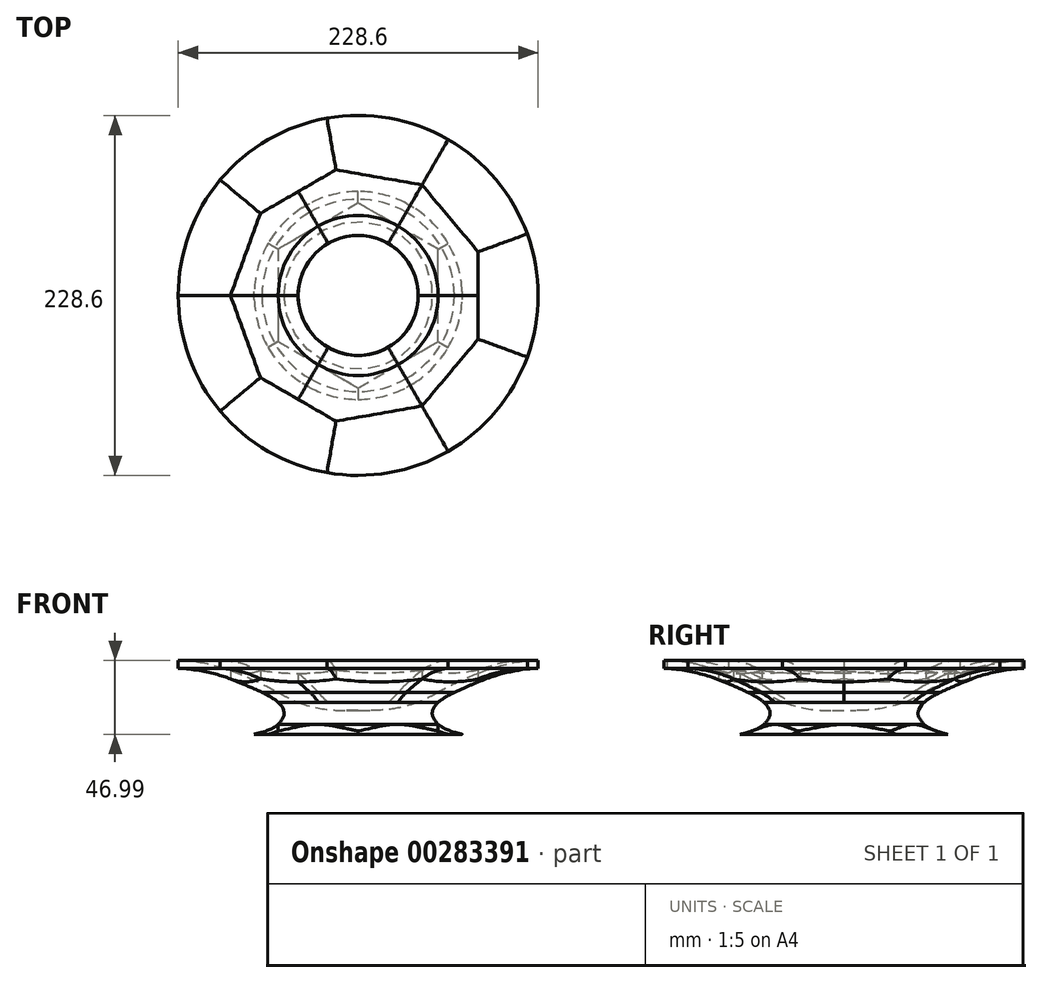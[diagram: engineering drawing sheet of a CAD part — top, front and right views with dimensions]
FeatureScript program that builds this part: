
annotation { "Feature Type Name" : "Feature", "Feature Type Description" : "" }
export const myFeature = defineFeature(function(context is Context, id is Id, definition is map)
    precondition{}
    {
        {
            var Q0;
            Q0=qCreatedBy(makeId("Top.planeOp"),FACE);
            var sketch = newSketch(context, id + "F0", { "sketchPlane" : qUnion([Q0])});
            skLineSegment(sketch, "E0", {"start": v(0, 0) * mm, "end": v(114.3, 0) * mm, "construction": true});
            skCircle(sketch, "E1.cCircle", {"center": v(0, 0) * mm, "radius": 114.3 * mm, "construction": true});
            skLineSegment(sketch, "E1.0", {"start": v(114.3, 41.6) * mm, "end": v(114.3, -41.6) * mm});
            skLineSegment(sketch, "E1.1", {"start": v(114.3, -41.6) * mm, "end": v(60.82, -105.34) * mm});
            skLineSegment(sketch, "E1.2", {"start": v(60.82, -105.34) * mm, "end": v(-21.12, -119.79) * mm});
            skLineSegment(sketch, "E1.3", {"start": v(-21.12, -119.79) * mm, "end": v(-93.18, -78.19) * mm});
            skLineSegment(sketch, "E1.4", {"start": v(-93.18, -78.19) * mm, "end": v(-121.64, 0) * mm});
            skLineSegment(sketch, "E1.5", {"start": v(-121.64, 0) * mm, "end": v(-93.18, 78.19) * mm});
            skLineSegment(sketch, "E1.6", {"start": v(-93.18, 78.19) * mm, "end": v(-21.12, 119.79) * mm});
            skLineSegment(sketch, "E1.7", {"start": v(-21.12, 119.79) * mm, "end": v(60.82, 105.34) * mm});
            skLineSegment(sketch, "E1.8", {"start": v(60.82, 105.34) * mm, "end": v(114.3, 41.6) * mm});
            skPoint(sketch, "E1.0.midPoint", {"position": v(114.3, 0) * mm});
            skLineSegment(sketch, "E2", {"start": v(114.3, 0) * mm, "end": v(76.2, 0) * mm, "construction": true});
            skCircle(sketch, "E3.cCircle", {"center": v(0, 0) * mm, "radius": 76.2 * mm, "construction": true});
            skLineSegment(sketch, "E3.0", {"start": v(76.2, 27.73) * mm, "end": v(76.2, -27.73) * mm});
            skLineSegment(sketch, "E3.1", {"start": v(76.2, -27.73) * mm, "end": v(40.55, -70.23) * mm});
            skLineSegment(sketch, "E3.2", {"start": v(40.55, -70.23) * mm, "end": v(-14.08, -79.86) * mm});
            skLineSegment(sketch, "E3.3", {"start": v(-14.08, -79.86) * mm, "end": v(-62.12, -52.12) * mm});
            skLineSegment(sketch, "E3.4", {"start": v(-62.12, -52.12) * mm, "end": v(-81.1, 0) * mm});
            skLineSegment(sketch, "E3.5", {"start": v(-81.1, 0) * mm, "end": v(-62.12, 52.12) * mm});
            skLineSegment(sketch, "E3.6", {"start": v(-62.12, 52.12) * mm, "end": v(-14.08, 79.86) * mm});
            skLineSegment(sketch, "E3.7", {"start": v(-14.08, 79.86) * mm, "end": v(40.55, 70.23) * mm});
            skLineSegment(sketch, "E3.8", {"start": v(40.55, 70.23) * mm, "end": v(76.2, 27.73) * mm});
            skPoint(sketch, "E3.0.midPoint", {"position": v(76.2, 0) * mm});
            skLineSegment(sketch, "E4", {"start": v(-21.12, 119.79) * mm, "end": v(-14.08, 79.86) * mm});
            skLineSegment(sketch, "E5", {"start": v(-93.18, 78.19) * mm, "end": v(-62.12, 52.12) * mm});
            skLineSegment(sketch, "E6", {"start": v(40.55, 70.23) * mm, "end": v(60.82, 105.34) * mm});
            skLineSegment(sketch, "E7", {"start": v(76.2, 27.73) * mm, "end": v(114.3, 41.6) * mm});
            skLineSegment(sketch, "E8", {"start": v(76.2, 0) * mm, "end": v(57.15, 0) * mm, "construction": true});
            skLineSegment(sketch, "E9", {"start": v(-62.12, 52.12) * mm, "end": v(-29.12, 33.07) * mm, "construction": true});
            skCircle(sketch, "E10.cCircle", {"center": v(0, 0) * mm, "radius": 48.23 * mm, "construction": true});
            skLineSegment(sketch, "E10.0", {"start": v(-48.23, 0) * mm, "end": v(-24.12, 41.77) * mm});
            skLineSegment(sketch, "E10.1", {"start": v(-24.12, 41.77) * mm, "end": v(24.12, 41.77) * mm});
            skLineSegment(sketch, "E10.2", {"start": v(24.12, 41.77) * mm, "end": v(48.23, 0) * mm});
            skLineSegment(sketch, "E10.3", {"start": v(48.23, 0) * mm, "end": v(24.12, -41.77) * mm});
            skLineSegment(sketch, "E10.4", {"start": v(24.12, -41.77) * mm, "end": v(-24.12, -41.77) * mm});
            skLineSegment(sketch, "E10.5", {"start": v(-24.12, -41.77) * mm, "end": v(-48.23, 0) * mm});
            skLineSegment(sketch, "E11", {"start": v(-81.1, 0) * mm, "end": v(-48.23, 0) * mm});
            skLineSegment(sketch, "E12", {"start": v(-24.12, 41.77) * mm, "end": v(-38.1, 66) * mm});
            skLineSegment(sketch, "E13", {"start": v(24.12, 41.77) * mm, "end": v(40.55, 70.23) * mm});
            skSolve(sketch);
        }
        {
            var Q0;
            Q0=makeQuery(id+"F0.imprint","IMPRINT",FACE,{"disambiguationData":[TD([[makeQuery(id+"F0.imprint","IMPRINT",EDGE,{"derivedFrom":sQuery(id+"F0.wireOp",EDGE,"E1.6")}),-1.0]])]});
            var Q1;
            Q1=makeQuery(id+"F0.imprint","IMPRINT",FACE,{"disambiguationData":[TD([[makeQuery(id+"F0.imprint","IMPRINT",EDGE,{"derivedFrom":sQuery(id+"F0.wireOp",EDGE,"E1.8")}),-1.0]])]});
            extrude(context, id + "F1", {"entities" : qUnion([Q0, Q1]), "depth" : 20.32 * mm, "offsetDistance" : 25.4 * mm});
        }
        {
            var Q0;
            {var subQ1=sQuery(id+"F0.wireOp",EDGE,"E3.5");Q0=makeQuery(id+"F0.imprint","IMPRINT",FACE,{"disambiguationData":[TD([[makeQuery(id+"F0.imprint","IMPRINT",EDGE,{"derivedFrom":subQ1}),-1.0]])]});}
            var Q1;
            Q1=makeQuery(id+"F0.imprint","IMPRINT",FACE,{"disambiguationData":[TD([[makeQuery(id+"F0.imprint","IMPRINT",EDGE,{"derivedFrom":sQuery(id+"F0.wireOp",EDGE,"E1.7")}),-1.0]])]});
            extrude(context, id + "F2", {"entities" : qUnion([Q0, Q1]), "depth" : 20.32 * mm});
        }
        {
            var Q0;
            {var subQ0=sQuery(id+"F0.wireOp",EDGE,"E3.7");Q0=makeQuery(id+"F0.imprint","IMPRINT",FACE,{"disambiguationData":[TD([[makeQuery(id+"F0.imprint","IMPRINT",EDGE,{"derivedFrom":subQ0}),-1.0]])]});}
            extrude(context, id + "F3", {"entities" : qUnion([Q0]), "depth" : 20.32 * mm});
        }
        {
            var Q0;
            Q0=qCreatedBy(makeId("Front.planeOp"),FACE);
            var sketch = newSketch(context, id + "F4", { "sketchPlane" : qUnion([Q0])});
            skLineSegment(sketch, "E14", {"start": v(0, 0) * mm, "end": v(0, 114.3) * mm, "construction": true});
            skSolve(sketch);
        }
        {
            var Q0;
            Q0=qCreatedBy(makeId("Top.planeOp"),FACE);
            var sketch = newSketch(context, id + "F5", { "sketchPlane" : qUnion([Q0])});
            skLineSegment(sketch, "E15", {"start": v(0, 0) * mm, "end": v(76.2, 0) * mm, "construction": true});
            skCircle(sketch, "E16.cCircle", {"center": v(0, 0) * mm, "radius": 76.2 * mm, "construction": true});
            skLineSegment(sketch, "E16.0", {"start": v(76.2, 0) * mm, "end": v(38.1, -66) * mm});
            skLineSegment(sketch, "E16.1", {"start": v(38.1, -66) * mm, "end": v(-38.1, -66) * mm});
            skLineSegment(sketch, "E16.2", {"start": v(-38.1, -66) * mm, "end": v(-76.2, 0) * mm});
            skLineSegment(sketch, "E16.3", {"start": v(-76.2, 0) * mm, "end": v(-38.1, 66) * mm});
            skLineSegment(sketch, "E16.4", {"start": v(-38.1, 66) * mm, "end": v(38.1, 66) * mm});
            skLineSegment(sketch, "E16.5", {"start": v(38.1, 66) * mm, "end": v(76.2, 0) * mm});
            skLineSegment(sketch, "E17", {"start": v(0, 0) * mm, "end": v(38.1, 0) * mm, "construction": true});
            skCircle(sketch, "E18.cCircle", {"center": v(0, 0) * mm, "radius": 38.1 * mm, "construction": true});
            skLineSegment(sketch, "E18.0", {"start": v(38.1, 0) * mm, "end": v(19.05, -33) * mm});
            skLineSegment(sketch, "E18.1", {"start": v(19.05, -33) * mm, "end": v(-19.05, -33) * mm});
            skLineSegment(sketch, "E18.2", {"start": v(-19.05, -33) * mm, "end": v(-38.1, 0) * mm});
            skLineSegment(sketch, "E18.3", {"start": v(-38.1, 0) * mm, "end": v(-19.05, 33) * mm});
            skLineSegment(sketch, "E18.4", {"start": v(-19.05, 33) * mm, "end": v(19.05, 33) * mm});
            skLineSegment(sketch, "E18.5", {"start": v(19.05, 33) * mm, "end": v(38.1, 0) * mm});
            skLineSegment(sketch, "E19", {"start": v(19.05, -33) * mm, "end": v(38.1, -66) * mm});
            skLineSegment(sketch, "E20", {"start": v(38.1, 0) * mm, "end": v(76.2, 0) * mm});
            skLineSegment(sketch, "E21", {"start": v(19.05, 33) * mm, "end": v(38.1, 66) * mm});
            skSolve(sketch);
        }
        {
            var Q0;
            Q0=makeQuery(id+"F5.imprint","IMPRINT",FACE,{"disambiguationData":[TD([[makeQuery(id+"F5.imprint","IMPRINT",EDGE,{"derivedFrom":sQuery(id+"F5.wireOp",EDGE,"E16.0")}),-1.0]])]});
            extrude(context, id + "F6", {"entities" : qUnion([Q0]), "oppositeDirection" : true, "depth" : 6.35 * mm});
        }
        {
            var Q0;
            Q0=makeQuery(id+"F5.imprint","IMPRINT",FACE,{"disambiguationData":[TD([[makeQuery(id+"F5.imprint","IMPRINT",EDGE,{"derivedFrom":sQuery(id+"F5.wireOp",EDGE,"E16.5")}),-1.0]])]});
            extrude(context, id + "F7", {"entities" : qUnion([Q0]), "oppositeDirection" : true, "depth" : 6.35 * mm});
        }
        {
            var Q0;
            Q0=makeQuery(id+"F6.opExtrude","SWEPT_BODY",BODY,{"disambiguationData":[OSD([sQuery(id+"F5.wireOp",EDGE,"E16.0"),sQuery(id+"F5.wireOp",EDGE,"E18.0"),sQuery(id+"F5.wireOp",EDGE,"E19"),sQuery(id+"F5.wireOp",EDGE,"E20")])]});
            var Q1;
            Q1=makeQuery(id+"F7.opExtrude","SWEPT_BODY",BODY,{"disambiguationData":[OSD([sQuery(id+"F5.wireOp",EDGE,"E16.5"),sQuery(id+"F5.wireOp",EDGE,"E18.5"),sQuery(id+"F5.wireOp",EDGE,"E20"),sQuery(id+"F5.wireOp",EDGE,"E21")])]});
            var Q2;
            Q2=sQuery(id+"F4.wireOp",EDGE,"E14");
            transform(context, id + "F8", {"entities" : qUnion([Q0, Q1]), "transformType" : TransformType.ROTATION, "transformAxis" : qUnion([Q2]), "angle" : 60 * degree, "makeCopy" : false});
        }
        {
            var Q0;
            Q0=makeQuery(id+"F2.opExtrude","SWEPT_BODY",BODY,{"disambiguationData":[OSD([sQuery(id+"F0.wireOp",EDGE,"E3.5"),sQuery(id+"F0.wireOp",EDGE,"E3.6"),sQuery(id+"F0.wireOp",EDGE,"201d4f59-2997-49bd-9f8f-c68fa2623fab.3"),sQuery(id+"F0.wireOp",EDGE,"vol62nw5-0ljN-dSfL-tH07-V83CAlSku6MR"),sQuery(id+"F0.wireOp",EDGE,"AOmgBGB9-Bh4F-KEFf-iWFI-fRoqLKZDZUkD")])]});
            var Q1;
            Q1=makeQuery(id+"F1.opExtrude","SWEPT_BODY",BODY,{"disambiguationData":[OSD([sQuery(id+"F0.wireOp",EDGE,"E1.8"),sQuery(id+"F0.wireOp",EDGE,"E3.8"),sQuery(id+"F0.wireOp",EDGE,"E6"),sQuery(id+"F0.wireOp",EDGE,"E7")])]});
            var Q2;
            Q2=makeQuery(id+"F3.opExtrude","SWEPT_BODY",BODY,{"disambiguationData":[OSD([sQuery(id+"F0.wireOp",EDGE,"E3.6"),sQuery(id+"F0.wireOp",EDGE,"E3.7"),sQuery(id+"F0.wireOp",EDGE,"201d4f59-2997-49bd-9f8f-c68fa2623fab.4"),sQuery(id+"F0.wireOp",EDGE,"h17IytfR-Qpnw-Sum6-dVJG-BEsi5LHsENnV"),sQuery(id+"F0.wireOp",EDGE,"vol62nw5-0ljN-dSfL-tH07-V83CAlSku6MR")])]});
            var Q3;
            Q3=makeQuery(id+"F2.opExtrude","SWEPT_BODY",BODY,{"disambiguationData":[OSD([sQuery(id+"F0.wireOp",EDGE,"E1.7"),sQuery(id+"F0.wireOp",EDGE,"E3.7"),sQuery(id+"F0.wireOp",EDGE,"E4"),sQuery(id+"F0.wireOp",EDGE,"E6")])]});
            var Q4;
            Q4=makeQuery(id+"F1.opExtrude","SWEPT_BODY",BODY,{"disambiguationData":[OSD([sQuery(id+"F0.wireOp",EDGE,"E1.6"),sQuery(id+"F0.wireOp",EDGE,"E3.6"),sQuery(id+"F0.wireOp",EDGE,"E4"),sQuery(id+"F0.wireOp",EDGE,"E5")])]});
            var Q5;
            Q5=makeQuery(id+"F6.opExtrude","SWEPT_BODY",BODY,{"disambiguationData":[OSD([sQuery(id+"F5.wireOp",EDGE,"E16.0"),sQuery(id+"F5.wireOp",EDGE,"E18.0"),sQuery(id+"F5.wireOp",EDGE,"E19"),sQuery(id+"F5.wireOp",EDGE,"E20")])]});
            var Q6;
            Q6=makeQuery(id+"F7.opExtrude","SWEPT_BODY",BODY,{"disambiguationData":[OSD([sQuery(id+"F5.wireOp",EDGE,"E16.5"),sQuery(id+"F5.wireOp",EDGE,"E18.5"),sQuery(id+"F5.wireOp",EDGE,"E20"),sQuery(id+"F5.wireOp",EDGE,"E21")])]});
            var Q7;
            Q7=sQuery(id+"F4.wireOp",EDGE,"E14");
            transform(context, id + "F9", {"entities" : qUnion([Q0, Q1, Q2, Q3, Q4, Q5, Q6]), "transformType" : TransformType.ROTATION, "transformAxis" : qUnion([Q7]), "angle" : 120 * degree, "makeCopy" : true});
        }
        {
            var Q0;
            Q0=makeQuery(id+"F2.opExtrude","SWEPT_BODY",BODY,{"disambiguationData":[OSD([sQuery(id+"F0.wireOp",EDGE,"E1.7"),sQuery(id+"F0.wireOp",EDGE,"E3.7"),sQuery(id+"F0.wireOp",EDGE,"E4"),sQuery(id+"F0.wireOp",EDGE,"E6")])]});
            var Q1;
            Q1=makeQuery(id+"F3.opExtrude","SWEPT_BODY",BODY,{"disambiguationData":[OSD([sQuery(id+"F0.wireOp",EDGE,"E3.6"),sQuery(id+"F0.wireOp",EDGE,"E3.7"),sQuery(id+"F0.wireOp",EDGE,"201d4f59-2997-49bd-9f8f-c68fa2623fab.4"),sQuery(id+"F0.wireOp",EDGE,"h17IytfR-Qpnw-Sum6-dVJG-BEsi5LHsENnV"),sQuery(id+"F0.wireOp",EDGE,"vol62nw5-0ljN-dSfL-tH07-V83CAlSku6MR")])]});
            var Q2;
            Q2=makeQuery(id+"F1.opExtrude","SWEPT_BODY",BODY,{"disambiguationData":[OSD([sQuery(id+"F0.wireOp",EDGE,"E1.6"),sQuery(id+"F0.wireOp",EDGE,"E3.6"),sQuery(id+"F0.wireOp",EDGE,"E4"),sQuery(id+"F0.wireOp",EDGE,"E5")])]});
            var Q3;
            Q3=makeQuery(id+"F2.opExtrude","SWEPT_BODY",BODY,{"disambiguationData":[OSD([sQuery(id+"F0.wireOp",EDGE,"E3.5"),sQuery(id+"F0.wireOp",EDGE,"E3.6"),sQuery(id+"F0.wireOp",EDGE,"201d4f59-2997-49bd-9f8f-c68fa2623fab.3"),sQuery(id+"F0.wireOp",EDGE,"vol62nw5-0ljN-dSfL-tH07-V83CAlSku6MR"),sQuery(id+"F0.wireOp",EDGE,"AOmgBGB9-Bh4F-KEFf-iWFI-fRoqLKZDZUkD")])]});
            var Q4;
            Q4=makeQuery(id+"F1.opExtrude","SWEPT_BODY",BODY,{"disambiguationData":[OSD([sQuery(id+"F0.wireOp",EDGE,"E1.8"),sQuery(id+"F0.wireOp",EDGE,"E3.8"),sQuery(id+"F0.wireOp",EDGE,"E6"),sQuery(id+"F0.wireOp",EDGE,"E7")])]});
            var Q5;
            Q5=makeQuery(id+"F6.opExtrude","SWEPT_BODY",BODY,{"disambiguationData":[OSD([sQuery(id+"F5.wireOp",EDGE,"E16.0"),sQuery(id+"F5.wireOp",EDGE,"E18.0"),sQuery(id+"F5.wireOp",EDGE,"E19"),sQuery(id+"F5.wireOp",EDGE,"E20")])]});
            var Q6;
            Q6=makeQuery(id+"F7.opExtrude","SWEPT_BODY",BODY,{"disambiguationData":[OSD([sQuery(id+"F5.wireOp",EDGE,"E16.5"),sQuery(id+"F5.wireOp",EDGE,"E18.5"),sQuery(id+"F5.wireOp",EDGE,"E20"),sQuery(id+"F5.wireOp",EDGE,"E21")])]});
            var Q7;
            Q7=sQuery(id+"F4.wireOp",EDGE,"E14");
            transform(context, id + "F10", {"entities" : qUnion([Q0, Q1, Q2, Q3, Q4, Q5, Q6]), "transformType" : TransformType.ROTATION, "transformAxis" : qUnion([Q7]), "angle" : 120 * degree, "oppositeDirection" : true, "makeCopy" : true});
        }
        {
            var Q0;
            Q0=makeQuery(id+"F9.opPattern","COPY",FACE,{"derivedFrom":makeQuery(id+"F7.opExtrude","CAP_FACE",FACE,{"disambiguationData":[OSD([sQuery(id+"F5.wireOp",EDGE,"E16.5"),sQuery(id+"F5.wireOp",EDGE,"E18.5"),sQuery(id+"F5.wireOp",EDGE,"E20"),sQuery(id+"F5.wireOp",EDGE,"E21")])],"isStart":false}),"instanceName":"1"});
            var sketch = newSketch(context, id + "F11", { "sketchPlane" : qUnion([Q0])});
            skLineSegment(sketch, "E22", {"start": v(-38.1, 66) * mm, "end": v(0, 0) * mm, "construction": true});
            skLineSegment(sketch, "E23", {"start": v(0, 0) * mm, "end": v(50.8, 0) * mm, "construction": true});
            skCircle(sketch, "E24.cCircle", {"center": v(0, 0) * mm, "radius": 50.8 * mm, "construction": true});
            skLineSegment(sketch, "E24.0", {"start": v(50.8, 29.33) * mm, "end": v(50.8, -29.33) * mm});
            skLineSegment(sketch, "E24.1", {"start": v(50.8, -29.33) * mm, "end": v(0, -58.66) * mm});
            skLineSegment(sketch, "E24.2", {"start": v(0, -58.66) * mm, "end": v(-50.8, -29.33) * mm});
            skLineSegment(sketch, "E24.3", {"start": v(-50.8, -29.33) * mm, "end": v(-50.8, 29.33) * mm});
            skLineSegment(sketch, "E24.4", {"start": v(-50.8, 29.33) * mm, "end": v(0, 58.66) * mm});
            skLineSegment(sketch, "E24.5", {"start": v(0, 58.66) * mm, "end": v(50.8, 29.33) * mm});
            skPoint(sketch, "E24.0.midPoint", {"position": v(50.8, 0) * mm});
            skSolve(sketch);
        }
        {
            var Q0;
            Q0 = qSketchRegion(id + "F11", true);
            extrude(context, id + "F12", {"entities" : qUnion([Q0]), "depth" : 20.32 * mm});
        }
        {
            var Q0;
            Q0=makeQuery(id+"F9.opPattern","COPY",BODY,{"derivedFrom":makeQuery(id+"F7.opExtrude","SWEPT_BODY",BODY,{"disambiguationData":[OSD([sQuery(id+"F5.wireOp",EDGE,"E16.5"),sQuery(id+"F5.wireOp",EDGE,"E18.5"),sQuery(id+"F5.wireOp",EDGE,"E20"),sQuery(id+"F5.wireOp",EDGE,"E21")])]}),"instanceName":"1"});
            var Q1;
            Q1=makeQuery(id+"F9.opPattern","COPY",BODY,{"derivedFrom":makeQuery(id+"F6.opExtrude","SWEPT_BODY",BODY,{"disambiguationData":[OSD([sQuery(id+"F5.wireOp",EDGE,"E16.0"),sQuery(id+"F5.wireOp",EDGE,"E18.0"),sQuery(id+"F5.wireOp",EDGE,"E19"),sQuery(id+"F5.wireOp",EDGE,"E20")])]}),"instanceName":"1"});
            var Q2;
            Q2=makeQuery(id+"F7.opExtrude","SWEPT_BODY",BODY,{"disambiguationData":[OSD([sQuery(id+"F5.wireOp",EDGE,"E16.5"),sQuery(id+"F5.wireOp",EDGE,"E18.5"),sQuery(id+"F5.wireOp",EDGE,"E20"),sQuery(id+"F5.wireOp",EDGE,"E21")])]});
            var Q3;
            Q3=makeQuery(id+"F6.opExtrude","SWEPT_BODY",BODY,{"disambiguationData":[OSD([sQuery(id+"F5.wireOp",EDGE,"E16.0"),sQuery(id+"F5.wireOp",EDGE,"E18.0"),sQuery(id+"F5.wireOp",EDGE,"E19"),sQuery(id+"F5.wireOp",EDGE,"E20")])]});
            var Q4;
            Q4=makeQuery(id+"F10.opPattern","COPY",BODY,{"derivedFrom":makeQuery(id+"F7.opExtrude","SWEPT_BODY",BODY,{"disambiguationData":[OSD([sQuery(id+"F5.wireOp",EDGE,"E16.5"),sQuery(id+"F5.wireOp",EDGE,"E18.5"),sQuery(id+"F5.wireOp",EDGE,"E20"),sQuery(id+"F5.wireOp",EDGE,"E21")])]}),"instanceName":"1"});
            var Q5;
            Q5=makeQuery(id+"F10.opPattern","COPY",BODY,{"derivedFrom":makeQuery(id+"F6.opExtrude","SWEPT_BODY",BODY,{"disambiguationData":[OSD([sQuery(id+"F5.wireOp",EDGE,"E16.0"),sQuery(id+"F5.wireOp",EDGE,"E18.0"),sQuery(id+"F5.wireOp",EDGE,"E19"),sQuery(id+"F5.wireOp",EDGE,"E20")])]}),"instanceName":"1"});
            transform(context, id + "F13", {"entities" : qUnion([Q0, Q1, Q2, Q3, Q4, Q5]), "transformType" : TransformType.TRANSLATION_3D, "dx" : 0 * mm, "dy" : 0 * mm, "dz" : -20.32 * mm, "makeCopy" : true});
        }
        {
            var Q0;
            Q0=makeQuery(id+"F13.opPattern","COPY",BODY,{"derivedFrom":makeQuery(id+"F9.opPattern","COPY",BODY,{"derivedFrom":makeQuery(id+"F6.opExtrude","SWEPT_BODY",BODY,{"disambiguationData":[OSD([sQuery(id+"F5.wireOp",EDGE,"E16.0"),sQuery(id+"F5.wireOp",EDGE,"E18.0"),sQuery(id+"F5.wireOp",EDGE,"E19"),sQuery(id+"F5.wireOp",EDGE,"E20")])]}),"instanceName":"1"}),"instanceName":"1"});
            var Q1;
            Q1=makeQuery(id+"F13.opPattern","COPY",BODY,{"derivedFrom":makeQuery(id+"F9.opPattern","COPY",BODY,{"derivedFrom":makeQuery(id+"F7.opExtrude","SWEPT_BODY",BODY,{"disambiguationData":[OSD([sQuery(id+"F5.wireOp",EDGE,"E16.5"),sQuery(id+"F5.wireOp",EDGE,"E18.5"),sQuery(id+"F5.wireOp",EDGE,"E20"),sQuery(id+"F5.wireOp",EDGE,"E21")])]}),"instanceName":"1"}),"instanceName":"1"});
            var Q2;
            Q2=makeQuery(id+"F13.opPattern","COPY",BODY,{"derivedFrom":makeQuery(id+"F10.opPattern","COPY",BODY,{"derivedFrom":makeQuery(id+"F6.opExtrude","SWEPT_BODY",BODY,{"disambiguationData":[OSD([sQuery(id+"F5.wireOp",EDGE,"E16.0"),sQuery(id+"F5.wireOp",EDGE,"E18.0"),sQuery(id+"F5.wireOp",EDGE,"E19"),sQuery(id+"F5.wireOp",EDGE,"E20")])]}),"instanceName":"1"}),"instanceName":"1"});
            var Q3;
            Q3=makeQuery(id+"F13.opPattern","COPY",BODY,{"derivedFrom":makeQuery(id+"F10.opPattern","COPY",BODY,{"derivedFrom":makeQuery(id+"F7.opExtrude","SWEPT_BODY",BODY,{"disambiguationData":[OSD([sQuery(id+"F5.wireOp",EDGE,"E16.5"),sQuery(id+"F5.wireOp",EDGE,"E18.5"),sQuery(id+"F5.wireOp",EDGE,"E20"),sQuery(id+"F5.wireOp",EDGE,"E21")])]}),"instanceName":"1"}),"instanceName":"1"});
            var Q4;
            Q4=makeQuery(id+"F13.opPattern","COPY",BODY,{"derivedFrom":makeQuery(id+"F6.opExtrude","SWEPT_BODY",BODY,{"disambiguationData":[OSD([sQuery(id+"F5.wireOp",EDGE,"E16.0"),sQuery(id+"F5.wireOp",EDGE,"E18.0"),sQuery(id+"F5.wireOp",EDGE,"E19"),sQuery(id+"F5.wireOp",EDGE,"E20")])]}),"instanceName":"1"});
            var Q5;
            Q5=makeQuery(id+"F13.opPattern","COPY",BODY,{"derivedFrom":makeQuery(id+"F7.opExtrude","SWEPT_BODY",BODY,{"disambiguationData":[OSD([sQuery(id+"F5.wireOp",EDGE,"E16.5"),sQuery(id+"F5.wireOp",EDGE,"E18.5"),sQuery(id+"F5.wireOp",EDGE,"E20"),sQuery(id+"F5.wireOp",EDGE,"E21")])]}),"instanceName":"1"});
            var Q6;
            Q6=sQuery(id+"F4.wireOp",EDGE,"E14");
            transform(context, id + "F14", {"entities" : qUnion([Q0, Q1, Q2, Q3, Q4, Q5]), "transformType" : TransformType.ROTATION, "transformAxis" : qUnion([Q6]), "angle" : 30 * degree, "makeCopy" : false});
        }
        {
            var Q0;
            Q0=makeQuery(id+"F12.opExtrude","SWEPT_BODY",BODY,{"disambiguationData":[OSD([sQuery(id+"F11.wireOp",EDGE,"E24.0"),sQuery(id+"F11.wireOp",EDGE,"E24.1"),sQuery(id+"F11.wireOp",EDGE,"E24.2"),sQuery(id+"F11.wireOp",EDGE,"E24.3"),sQuery(id+"F11.wireOp",EDGE,"E24.4"),sQuery(id+"F11.wireOp",EDGE,"E24.5")])]});
            var Q1;
            Q1=makeQuery(id+"F13.opPattern","COPY",BODY,{"derivedFrom":makeQuery(id+"F9.opPattern","COPY",BODY,{"derivedFrom":makeQuery(id+"F7.opExtrude","SWEPT_BODY",BODY,{"disambiguationData":[OSD([sQuery(id+"F5.wireOp",EDGE,"E16.5"),sQuery(id+"F5.wireOp",EDGE,"E18.5"),sQuery(id+"F5.wireOp",EDGE,"E20"),sQuery(id+"F5.wireOp",EDGE,"E21")])]}),"instanceName":"1"}),"instanceName":"1"});
            var Q2;
            Q2=makeQuery(id+"F13.opPattern","COPY",BODY,{"derivedFrom":makeQuery(id+"F10.opPattern","COPY",BODY,{"derivedFrom":makeQuery(id+"F6.opExtrude","SWEPT_BODY",BODY,{"disambiguationData":[OSD([sQuery(id+"F5.wireOp",EDGE,"E16.0"),sQuery(id+"F5.wireOp",EDGE,"E18.0"),sQuery(id+"F5.wireOp",EDGE,"E19"),sQuery(id+"F5.wireOp",EDGE,"E20")])]}),"instanceName":"1"}),"instanceName":"1"});
            var Q3;
            Q3=makeQuery(id+"F13.opPattern","COPY",BODY,{"derivedFrom":makeQuery(id+"F10.opPattern","COPY",BODY,{"derivedFrom":makeQuery(id+"F7.opExtrude","SWEPT_BODY",BODY,{"disambiguationData":[OSD([sQuery(id+"F5.wireOp",EDGE,"E16.5"),sQuery(id+"F5.wireOp",EDGE,"E18.5"),sQuery(id+"F5.wireOp",EDGE,"E20"),sQuery(id+"F5.wireOp",EDGE,"E21")])]}),"instanceName":"1"}),"instanceName":"1"});
            var Q4;
            Q4=makeQuery(id+"F13.opPattern","COPY",BODY,{"derivedFrom":makeQuery(id+"F6.opExtrude","SWEPT_BODY",BODY,{"disambiguationData":[OSD([sQuery(id+"F5.wireOp",EDGE,"E16.0"),sQuery(id+"F5.wireOp",EDGE,"E18.0"),sQuery(id+"F5.wireOp",EDGE,"E19"),sQuery(id+"F5.wireOp",EDGE,"E20")])]}),"instanceName":"1"});
            var Q5;
            Q5=makeQuery(id+"F13.opPattern","COPY",BODY,{"derivedFrom":makeQuery(id+"F7.opExtrude","SWEPT_BODY",BODY,{"disambiguationData":[OSD([sQuery(id+"F5.wireOp",EDGE,"E16.5"),sQuery(id+"F5.wireOp",EDGE,"E18.5"),sQuery(id+"F5.wireOp",EDGE,"E20"),sQuery(id+"F5.wireOp",EDGE,"E21")])]}),"instanceName":"1"});
            var Q6;
            Q6=makeQuery(id+"F13.opPattern","COPY",BODY,{"derivedFrom":makeQuery(id+"F9.opPattern","COPY",BODY,{"derivedFrom":makeQuery(id+"F6.opExtrude","SWEPT_BODY",BODY,{"disambiguationData":[OSD([sQuery(id+"F5.wireOp",EDGE,"E16.0"),sQuery(id+"F5.wireOp",EDGE,"E18.0"),sQuery(id+"F5.wireOp",EDGE,"E19"),sQuery(id+"F5.wireOp",EDGE,"E20")])]}),"instanceName":"1"}),"instanceName":"1"});
            booleanBodies(context, id + "F15", {"operationType" : BooleanOperationType.SUBTRACTION, "tools" : qUnion([Q0]), "targets" : qUnion([Q1, Q2, Q3, Q4, Q5, Q6]), "keepTools" : true});
        }
        {
            var Q0;
            Q0=qCreatedBy(makeId("Right.planeOp"),FACE);
            var sketch = newSketch(context, id + "F16", { "sketchPlane" : qUnion([Q0])});
            skLineSegment(sketch, "E25", {"start": v(0, 0) * mm, "end": v(-114.3, 0) * mm, "construction": true});
            skLineSegment(sketch, "E26", {"start": v(-114.3, 0) * mm, "end": v(-114.3, 20.32) * mm, "construction": true});
            skLineSegment(sketch, "E27", {"start": v(-114.3, 20.32) * mm, "end": v(-50.8, 20.32) * mm, "construction": true});
            skLineSegment(sketch, "E28", {"start": v(-50.8, 20.32) * mm, "end": v(-50.8, 0) * mm, "construction": true});
            skLineSegment(sketch, "E29", {"start": v(-50.8, 0) * mm, "end": v(-38.1, 0) * mm, "construction": true});
            skLineSegment(sketch, "E30", {"start": v(-38.1, 0) * mm, "end": v(-38.1, -6.35) * mm, "construction": true});
            skLineSegment(sketch, "E31", {"start": v(-38.1, -6.35) * mm, "end": v(-38.1, -26.67) * mm, "construction": true});
            skLineSegment(sketch, "E32", {"start": v(-38.1, -26.67) * mm, "end": v(-63.5, -26.67) * mm, "construction": true});
            skLineSegment(sketch, "E33", {"start": v(-63.5, -26.67) * mm, "end": v(-63.5, -20.32) * mm, "construction": true});
            skLineSegment(sketch, "E34", {"start": v(-63.5, -20.32) * mm, "end": v(-50.8, -20.32) * mm, "construction": true});
            skLineSegment(sketch, "E35", {"start": v(-50.8, -20.32) * mm, "end": v(-50.8, -6.35) * mm, "construction": true});
            skLineSegment(sketch, "E36", {"start": v(-114.3, 20.32) * mm, "end": v(-114.3, 15.24) * mm, "construction": true});
            skFitSpline(sketch, "E37", {"points": [v(-50.8, -20.32) * mm, v(-47.07, -14.19) * mm, v(-50.8, -6.35) * mm, v(-70.87, 4.38) * mm, v(-85.96, 10.28) * mm, v(-114.3, 15.24) * mm], "startDerivative": vector(37.86, 43.28) * mm, "endDerivative": vector(-120.47, 2.36) * mm});
            skLineSegment(sketch, "E38", {"start": v(-38.1, -6.35) * mm, "end": v(0, -6.35) * mm, "construction": true});
            skLineSegment(sketch, "E39", {"start": v(0, -6.35) * mm, "end": v(0, -11.43) * mm, "construction": true});
            skFitSpline(sketch, "E40", {"points": [v(-114.3, 20.32) * mm, v(-71.06, 9.96) * mm, v(-50.8, 0) * mm, v(-38.1, -6.35) * mm, v(-21.02, -10.68) * mm, v(0, -11.43) * mm], "startDerivative": vector(181.54, 0) * mm, "endDerivative": vector(157.86, 2.62) * mm});
            skLineSegment(sketch, "E41", {"start": v(-38.1, -26.67) * mm, "end": v(-66.04, -26.67) * mm, "construction": true});
            skFitSpline(sketch, "E42", {"points": [v(-50.8, -20.32) * mm, v(-66.04, -26.67) * mm], "startDerivative": vector(-11.2, -9.67) * mm, "endDerivative": vector(-18.41, -4.56) * mm});
            skLineSegment(sketch, "E43", {"start": v(-66.04, -26.67) * mm, "end": v(0, -26.67) * mm});
            skLineSegment(sketch, "E44", {"start": v(0, -26.67) * mm, "end": v(0, -11.43) * mm});
            skLineSegment(sketch, "E45", {"start": v(-114.3, 20.32) * mm, "end": v(-114.3, 15.24) * mm});
            skSolve(sketch);
        }
        {
            var Q0;
            Q0 = qSketchRegion(id + "F16", true);
            var Q1;
            Q1=sQuery(id+"F4.wireOp",EDGE,"E14");
            revolve(context, id + "F17", {"entities" : qUnion([Q0]), "axis" : qUnion([Q1]), "revolveType" : RevolveType.FULL});
        }
        {
            var Q0;
            Q0=makeQuery(id+"F17.opRevolve","SWEPT_BODY",BODY,{"disambiguationData":[OSD([sQuery(id+"F16.wireOp",EDGE,"E37"),sQuery(id+"F16.wireOp",EDGE,"E40"),sQuery(id+"F16.wireOp",EDGE,"E42"),sQuery(id+"F16.wireOp",EDGE,"E43"),sQuery(id+"F16.wireOp",EDGE,"E44"),sQuery(id+"F16.wireOp",EDGE,"E45")])]});
            transform(context, id + "F18", {"entities" : qUnion([Q0]), "transformType" : TransformType.TRANSLATION_3D, "dx" : 0 * mm, "dy" : 304.8 * mm, "dz" : 0 * mm, "makeCopy" : false});
        }
        {
            var Q0;
            Q0=makeQuery(id+"F17.opRevolve","SWEPT_FACE",FACE,{"disambiguationData":[OSD([sQuery(id+"F16.wireOp",EDGE,"E43")])]});
            var sketch = newSketch(context, id + "F19", { "sketchPlane" : qUnion([Q0])});
            skLineSegment(sketch, "E46.bottom", {"start": v(-152.4, -155.9) * mm, "end": v(152.4, -155.9) * mm});
            skLineSegment(sketch, "E46.top", {"start": v(-152.4, 148.9) * mm, "end": v(152.4, 148.9) * mm});
            skLineSegment(sketch, "E46.left", {"start": v(-152.4, -155.9) * mm, "end": v(-152.4, 148.9) * mm});
            skLineSegment(sketch, "E46.right", {"start": v(152.4, -155.9) * mm, "end": v(152.4, 148.9) * mm});
            skPoint(sketch, "E46.middle", {"position": v(0, -3.5) * mm});
            skSolve(sketch);
        }
        {
            var Q0;
            Q0=makeQuery(id+"F19.imprint","IMPRINT",FACE,{"disambiguationData":[TD([[makeQuery(id+"F19.imprint","IMPRINT",EDGE,{"derivedFrom":sQuery(id+"F19.wireOp",EDGE,"E46.bottom")}),1.0]])]});
            extrude(context, id + "F20", {"entities" : qUnion([Q0]), "oppositeDirection" : true, "depth" : 47 * mm});
        }
        {
            var Q0;
            Q0=makeQuery(id+"F22.opBoolean","SPLIT",BODY,{"disambiguationData":[OD(0.0)],"derivedFrom":makeQuery(id+"F20.opExtrude","SWEPT_BODY",BODY,{"disambiguationData":[OSD([sQuery(id+"F16.wireOp",EDGE,"E42"),sQuery(id+"F16.wireOp",EDGE,"E43"),sQuery(id+"F19.wireOp",EDGE,"E46.bottom"),sQuery(id+"F19.wireOp",EDGE,"E46.top"),sQuery(id+"F19.wireOp",EDGE,"E46.left"),sQuery(id+"F19.wireOp",EDGE,"E46.right")])]})});
            var Q1;
            Q1=makeQuery(id+"F22.opBoolean","SPLIT",BODY,{"disambiguationData":[OD(1.0)],"derivedFrom":makeQuery(id+"F20.opExtrude","SWEPT_BODY",BODY,{"disambiguationData":[OSD([sQuery(id+"F16.wireOp",EDGE,"E42"),sQuery(id+"F16.wireOp",EDGE,"E43"),sQuery(id+"F19.wireOp",EDGE,"E46.bottom"),sQuery(id+"F19.wireOp",EDGE,"E46.top"),sQuery(id+"F19.wireOp",EDGE,"E46.left"),sQuery(id+"F19.wireOp",EDGE,"E46.right")])]})});
            transform(context, id + "F21", {"entities" : qUnion([Q0, Q1]), "transformType" : TransformType.TRANSLATION_3D, "dx" : 0 * mm, "dy" : 304.8 * mm, "dz" : 0 * mm, "makeCopy" : false});
        }
        {
            var Q0;
            Q0=makeQuery(id+"F17.opRevolve","SWEPT_BODY",BODY,{"disambiguationData":[OSD([sQuery(id+"F16.wireOp",EDGE,"E37"),sQuery(id+"F16.wireOp",EDGE,"E40"),sQuery(id+"F16.wireOp",EDGE,"E42"),sQuery(id+"F16.wireOp",EDGE,"E43"),sQuery(id+"F16.wireOp",EDGE,"E44"),sQuery(id+"F16.wireOp",EDGE,"E45")])]});
            var Q1;
            Q1=makeQuery(id+"F20.opExtrude","SWEPT_BODY",BODY,{"disambiguationData":[OSD([sQuery(id+"F19.wireOp",EDGE,"E46.bottom"),sQuery(id+"F19.wireOp",EDGE,"E46.top"),sQuery(id+"F19.wireOp",EDGE,"E46.left"),sQuery(id+"F19.wireOp",EDGE,"E46.right")])]});
            booleanBodies(context, id + "F22", {"operationType" : BooleanOperationType.SUBTRACTION, "tools" : qUnion([Q0]), "targets" : qUnion([Q1])});
        }
        {
            var Q0;
            Q0=makeQuery(id+"F22.opBoolean","SPLIT",BODY,{"disambiguationData":[OD(1.0)],"derivedFrom":makeQuery(id+"F20.opExtrude","SWEPT_BODY",BODY,{"disambiguationData":[OSD([sQuery(id+"F19.wireOp",EDGE,"E46.bottom"),sQuery(id+"F19.wireOp",EDGE,"E46.top"),sQuery(id+"F19.wireOp",EDGE,"E46.left"),sQuery(id+"F19.wireOp",EDGE,"E46.right")])]})});
            var Q1;
            Q1=makeQuery(id+"F22.opBoolean","SPLIT",BODY,{"disambiguationData":[OD(0.0)],"derivedFrom":makeQuery(id+"F20.opExtrude","SWEPT_BODY",BODY,{"disambiguationData":[OSD([sQuery(id+"F19.wireOp",EDGE,"E46.bottom"),sQuery(id+"F19.wireOp",EDGE,"E46.top"),sQuery(id+"F19.wireOp",EDGE,"E46.left"),sQuery(id+"F19.wireOp",EDGE,"E46.right")])]})});
            transform(context, id + "F23", {"entities" : qUnion([Q0, Q1]), "transformType" : TransformType.TRANSLATION_3D, "dx" : 0 * mm, "dy" : -304.8 * mm, "dz" : 0 * mm, "makeCopy" : false});
        }
        {
            var Q0;
            Q0=makeQuery(id+"F22.opBoolean","SPLIT",BODY,{"disambiguationData":[OD(1.0)],"derivedFrom":makeQuery(id+"F20.opExtrude","SWEPT_BODY",BODY,{"disambiguationData":[OSD([sQuery(id+"F16.wireOp",EDGE,"E42"),sQuery(id+"F16.wireOp",EDGE,"E43"),sQuery(id+"F19.wireOp",EDGE,"E46.bottom"),sQuery(id+"F19.wireOp",EDGE,"E46.top"),sQuery(id+"F19.wireOp",EDGE,"E46.left"),sQuery(id+"F19.wireOp",EDGE,"E46.right")])]})});
            var Q1;
            Q1=makeQuery(id+"F22.opBoolean","SPLIT",BODY,{"disambiguationData":[OD(0.0)],"derivedFrom":makeQuery(id+"F20.opExtrude","SWEPT_BODY",BODY,{"disambiguationData":[OSD([sQuery(id+"F16.wireOp",EDGE,"E42"),sQuery(id+"F16.wireOp",EDGE,"E43"),sQuery(id+"F19.wireOp",EDGE,"E46.bottom"),sQuery(id+"F19.wireOp",EDGE,"E46.top"),sQuery(id+"F19.wireOp",EDGE,"E46.left"),sQuery(id+"F19.wireOp",EDGE,"E46.right")])]})});
            var Q2;
            Q2=makeQuery(id+"F1.opExtrude","SWEPT_BODY",BODY,{"disambiguationData":[OSD([sQuery(id+"F0.wireOp",EDGE,"E1.6"),sQuery(id+"F0.wireOp",EDGE,"E3.6"),sQuery(id+"F0.wireOp",EDGE,"E4"),sQuery(id+"F0.wireOp",EDGE,"E5")])]});
            var Q3;
            Q3=makeQuery(id+"F13.opPattern","COPY",BODY,{"derivedFrom":makeQuery(id+"F10.opPattern","COPY",BODY,{"derivedFrom":makeQuery(id+"F7.opExtrude","SWEPT_BODY",BODY,{"disambiguationData":[OSD([sQuery(id+"F5.wireOp",EDGE,"E16.5"),sQuery(id+"F5.wireOp",EDGE,"E18.5"),sQuery(id+"F5.wireOp",EDGE,"E20"),sQuery(id+"F5.wireOp",EDGE,"E21")])]}),"instanceName":"1"}),"instanceName":"1"});
            var Q4;
            Q4=makeQuery(id+"F13.opPattern","COPY",BODY,{"derivedFrom":makeQuery(id+"F9.opPattern","COPY",BODY,{"derivedFrom":makeQuery(id+"F6.opExtrude","SWEPT_BODY",BODY,{"disambiguationData":[OSD([sQuery(id+"F5.wireOp",EDGE,"E16.0"),sQuery(id+"F5.wireOp",EDGE,"E18.0"),sQuery(id+"F5.wireOp",EDGE,"E19"),sQuery(id+"F5.wireOp",EDGE,"E20")])]}),"instanceName":"1"}),"instanceName":"1"});
            var Q5;
            Q5=makeQuery(id+"F13.opPattern","COPY",BODY,{"derivedFrom":makeQuery(id+"F9.opPattern","COPY",BODY,{"derivedFrom":makeQuery(id+"F7.opExtrude","SWEPT_BODY",BODY,{"disambiguationData":[OSD([sQuery(id+"F5.wireOp",EDGE,"E16.5"),sQuery(id+"F5.wireOp",EDGE,"E18.5"),sQuery(id+"F5.wireOp",EDGE,"E20"),sQuery(id+"F5.wireOp",EDGE,"E21")])]}),"instanceName":"1"}),"instanceName":"1"});
            var Q6;
            Q6=makeQuery(id+"F13.opPattern","COPY",BODY,{"derivedFrom":makeQuery(id+"F10.opPattern","COPY",BODY,{"derivedFrom":makeQuery(id+"F6.opExtrude","SWEPT_BODY",BODY,{"disambiguationData":[OSD([sQuery(id+"F5.wireOp",EDGE,"E16.0"),sQuery(id+"F5.wireOp",EDGE,"E18.0"),sQuery(id+"F5.wireOp",EDGE,"E19"),sQuery(id+"F5.wireOp",EDGE,"E20")])]}),"instanceName":"1"}),"instanceName":"1"});
            var Q7;
            Q7=makeQuery(id+"F13.opPattern","COPY",BODY,{"derivedFrom":makeQuery(id+"F7.opExtrude","SWEPT_BODY",BODY,{"disambiguationData":[OSD([sQuery(id+"F5.wireOp",EDGE,"E16.5"),sQuery(id+"F5.wireOp",EDGE,"E18.5"),sQuery(id+"F5.wireOp",EDGE,"E20"),sQuery(id+"F5.wireOp",EDGE,"E21")])]}),"instanceName":"1"});
            var Q8;
            Q8=makeQuery(id+"F3.opExtrude","SWEPT_BODY",BODY,{"disambiguationData":[OSD([sQuery(id+"F0.wireOp",EDGE,"E3.6"),sQuery(id+"F0.wireOp",EDGE,"E3.7"),sQuery(id+"F0.wireOp",EDGE,"E10.1"),sQuery(id+"F0.wireOp",EDGE,"E12"),sQuery(id+"F0.wireOp",EDGE,"E13")])]});
            var Q9;
            Q9=makeQuery(id+"F6.opExtrude","SWEPT_BODY",BODY,{"disambiguationData":[OSD([sQuery(id+"F5.wireOp",EDGE,"E16.0"),sQuery(id+"F5.wireOp",EDGE,"E18.0"),sQuery(id+"F5.wireOp",EDGE,"E19"),sQuery(id+"F5.wireOp",EDGE,"E20")])]});
            var Q10;
            Q10=makeQuery(id+"F7.opExtrude","SWEPT_BODY",BODY,{"disambiguationData":[OSD([sQuery(id+"F5.wireOp",EDGE,"E16.5"),sQuery(id+"F5.wireOp",EDGE,"E18.5"),sQuery(id+"F5.wireOp",EDGE,"E20"),sQuery(id+"F5.wireOp",EDGE,"E21")])]});
            var Q11;
            Q11=makeQuery(id+"F9.opPattern","COPY",BODY,{"derivedFrom":makeQuery(id+"F1.opExtrude","SWEPT_BODY",BODY,{"disambiguationData":[OSD([sQuery(id+"F0.wireOp",EDGE,"E1.6"),sQuery(id+"F0.wireOp",EDGE,"E3.6"),sQuery(id+"F0.wireOp",EDGE,"E4"),sQuery(id+"F0.wireOp",EDGE,"E5")])]}),"instanceName":"1"});
            var Q12;
            Q12=makeQuery(id+"F9.opPattern","COPY",BODY,{"derivedFrom":makeQuery(id+"F1.opExtrude","SWEPT_BODY",BODY,{"disambiguationData":[OSD([sQuery(id+"F0.wireOp",EDGE,"E1.8"),sQuery(id+"F0.wireOp",EDGE,"E3.8"),sQuery(id+"F0.wireOp",EDGE,"E6"),sQuery(id+"F0.wireOp",EDGE,"E7")])]}),"instanceName":"1"});
            var Q13;
            Q13=makeQuery(id+"F9.opPattern","COPY",BODY,{"derivedFrom":makeQuery(id+"F2.opExtrude","SWEPT_BODY",BODY,{"disambiguationData":[OSD([sQuery(id+"F0.wireOp",EDGE,"E1.7"),sQuery(id+"F0.wireOp",EDGE,"E3.7"),sQuery(id+"F0.wireOp",EDGE,"E4"),sQuery(id+"F0.wireOp",EDGE,"E6")])]}),"instanceName":"1"});
            var Q14;
            Q14=makeQuery(id+"F9.opPattern","COPY",BODY,{"derivedFrom":makeQuery(id+"F2.opExtrude","SWEPT_BODY",BODY,{"disambiguationData":[OSD([sQuery(id+"F0.wireOp",EDGE,"E3.5"),sQuery(id+"F0.wireOp",EDGE,"E3.6"),sQuery(id+"F0.wireOp",EDGE,"E10.0"),sQuery(id+"F0.wireOp",EDGE,"E11"),sQuery(id+"F0.wireOp",EDGE,"E12")])]}),"instanceName":"1"});
            var Q15;
            Q15=makeQuery(id+"F9.opPattern","COPY",BODY,{"derivedFrom":makeQuery(id+"F3.opExtrude","SWEPT_BODY",BODY,{"disambiguationData":[OSD([sQuery(id+"F0.wireOp",EDGE,"E3.6"),sQuery(id+"F0.wireOp",EDGE,"E3.7"),sQuery(id+"F0.wireOp",EDGE,"E10.1"),sQuery(id+"F0.wireOp",EDGE,"E12"),sQuery(id+"F0.wireOp",EDGE,"E13")])]}),"instanceName":"1"});
            var Q16;
            Q16=makeQuery(id+"F9.opPattern","COPY",BODY,{"derivedFrom":makeQuery(id+"F6.opExtrude","SWEPT_BODY",BODY,{"disambiguationData":[OSD([sQuery(id+"F5.wireOp",EDGE,"E16.0"),sQuery(id+"F5.wireOp",EDGE,"E18.0"),sQuery(id+"F5.wireOp",EDGE,"E19"),sQuery(id+"F5.wireOp",EDGE,"E20")])]}),"instanceName":"1"});
            var Q17;
            Q17=makeQuery(id+"F9.opPattern","COPY",BODY,{"derivedFrom":makeQuery(id+"F7.opExtrude","SWEPT_BODY",BODY,{"disambiguationData":[OSD([sQuery(id+"F5.wireOp",EDGE,"E16.5"),sQuery(id+"F5.wireOp",EDGE,"E18.5"),sQuery(id+"F5.wireOp",EDGE,"E20"),sQuery(id+"F5.wireOp",EDGE,"E21")])]}),"instanceName":"1"});
            var Q18;
            Q18=makeQuery(id+"F10.opPattern","COPY",BODY,{"derivedFrom":makeQuery(id+"F1.opExtrude","SWEPT_BODY",BODY,{"disambiguationData":[OSD([sQuery(id+"F0.wireOp",EDGE,"E1.6"),sQuery(id+"F0.wireOp",EDGE,"E3.6"),sQuery(id+"F0.wireOp",EDGE,"E4"),sQuery(id+"F0.wireOp",EDGE,"E5")])]}),"instanceName":"1"});
            var Q19;
            Q19=makeQuery(id+"F10.opPattern","COPY",BODY,{"derivedFrom":makeQuery(id+"F1.opExtrude","SWEPT_BODY",BODY,{"disambiguationData":[OSD([sQuery(id+"F0.wireOp",EDGE,"E1.8"),sQuery(id+"F0.wireOp",EDGE,"E3.8"),sQuery(id+"F0.wireOp",EDGE,"E6"),sQuery(id+"F0.wireOp",EDGE,"E7")])]}),"instanceName":"1"});
            var Q20;
            Q20=makeQuery(id+"F10.opPattern","COPY",BODY,{"derivedFrom":makeQuery(id+"F2.opExtrude","SWEPT_BODY",BODY,{"disambiguationData":[OSD([sQuery(id+"F0.wireOp",EDGE,"E1.7"),sQuery(id+"F0.wireOp",EDGE,"E3.7"),sQuery(id+"F0.wireOp",EDGE,"E4"),sQuery(id+"F0.wireOp",EDGE,"E6")])]}),"instanceName":"1"});
            var Q21;
            Q21=makeQuery(id+"F10.opPattern","COPY",BODY,{"derivedFrom":makeQuery(id+"F2.opExtrude","SWEPT_BODY",BODY,{"disambiguationData":[OSD([sQuery(id+"F0.wireOp",EDGE,"E3.5"),sQuery(id+"F0.wireOp",EDGE,"E3.6"),sQuery(id+"F0.wireOp",EDGE,"E10.0"),sQuery(id+"F0.wireOp",EDGE,"E11"),sQuery(id+"F0.wireOp",EDGE,"E12")])]}),"instanceName":"1"});
            var Q22;
            Q22=makeQuery(id+"F10.opPattern","COPY",BODY,{"derivedFrom":makeQuery(id+"F3.opExtrude","SWEPT_BODY",BODY,{"disambiguationData":[OSD([sQuery(id+"F0.wireOp",EDGE,"E3.6"),sQuery(id+"F0.wireOp",EDGE,"E3.7"),sQuery(id+"F0.wireOp",EDGE,"E10.1"),sQuery(id+"F0.wireOp",EDGE,"E12"),sQuery(id+"F0.wireOp",EDGE,"E13")])]}),"instanceName":"1"});
            var Q23;
            Q23=makeQuery(id+"F10.opPattern","COPY",BODY,{"derivedFrom":makeQuery(id+"F6.opExtrude","SWEPT_BODY",BODY,{"disambiguationData":[OSD([sQuery(id+"F5.wireOp",EDGE,"E16.0"),sQuery(id+"F5.wireOp",EDGE,"E18.0"),sQuery(id+"F5.wireOp",EDGE,"E19"),sQuery(id+"F5.wireOp",EDGE,"E20")])]}),"instanceName":"1"});
            var Q24;
            Q24=makeQuery(id+"F10.opPattern","COPY",BODY,{"derivedFrom":makeQuery(id+"F7.opExtrude","SWEPT_BODY",BODY,{"disambiguationData":[OSD([sQuery(id+"F5.wireOp",EDGE,"E16.5"),sQuery(id+"F5.wireOp",EDGE,"E18.5"),sQuery(id+"F5.wireOp",EDGE,"E20"),sQuery(id+"F5.wireOp",EDGE,"E21")])]}),"instanceName":"1"});
            var Q25;
            Q25=makeQuery(id+"F12.opExtrude","SWEPT_BODY",BODY,{"disambiguationData":[OSD([sQuery(id+"F11.wireOp",EDGE,"F9wYINEq-b9Sr-hUmB-xtWT-niWzykIYEAiM")])]});
            var Q26;
            Q26=makeQuery(id+"F13.opPattern","COPY",BODY,{"derivedFrom":makeQuery(id+"F6.opExtrude","SWEPT_BODY",BODY,{"disambiguationData":[OSD([sQuery(id+"F5.wireOp",EDGE,"E16.0"),sQuery(id+"F5.wireOp",EDGE,"E18.0"),sQuery(id+"F5.wireOp",EDGE,"E19"),sQuery(id+"F5.wireOp",EDGE,"E20")])]}),"instanceName":"1"});
            var Q27;
            Q27=makeQuery(id+"F1.opExtrude","SWEPT_BODY",BODY,{"disambiguationData":[OSD([sQuery(id+"F0.wireOp",EDGE,"E1.8"),sQuery(id+"F0.wireOp",EDGE,"E3.8"),sQuery(id+"F0.wireOp",EDGE,"E6"),sQuery(id+"F0.wireOp",EDGE,"E7")])]});
            var Q28;
            Q28=makeQuery(id+"F2.opExtrude","SWEPT_BODY",BODY,{"disambiguationData":[OSD([sQuery(id+"F0.wireOp",EDGE,"E1.7"),sQuery(id+"F0.wireOp",EDGE,"E3.7"),sQuery(id+"F0.wireOp",EDGE,"E4"),sQuery(id+"F0.wireOp",EDGE,"E6")])]});
            var Q29;
            Q29=makeQuery(id+"F2.opExtrude","SWEPT_BODY",BODY,{"disambiguationData":[OSD([sQuery(id+"F0.wireOp",EDGE,"E3.5"),sQuery(id+"F0.wireOp",EDGE,"E3.6"),sQuery(id+"F0.wireOp",EDGE,"E10.0"),sQuery(id+"F0.wireOp",EDGE,"E11"),sQuery(id+"F0.wireOp",EDGE,"E12")])]});
            var Q30;
            Q30=makeQuery(id+"F12.opExtrude","SWEPT_BODY",BODY,{"disambiguationData":[OSD([sQuery(id+"F11.wireOp",EDGE,"E24.0"),sQuery(id+"F11.wireOp",EDGE,"E24.1"),sQuery(id+"F11.wireOp",EDGE,"E24.2"),sQuery(id+"F11.wireOp",EDGE,"E24.3"),sQuery(id+"F11.wireOp",EDGE,"E24.4"),sQuery(id+"F11.wireOp",EDGE,"E24.5")])]});
            booleanBodies(context, id + "F24", {"operationType" : BooleanOperationType.SUBTRACTION, "tools" : qUnion([Q0, Q1]), "targets" : qUnion([Q2, Q3, Q4, Q5, Q6, Q7, Q8, Q9, Q10, Q11, Q12, Q13, Q14, Q15, Q16, Q17, Q18, Q19, Q20, Q21, Q22, Q23, Q24, Q25, Q26, Q27, Q28, Q29, Q30])});
        }
    });
